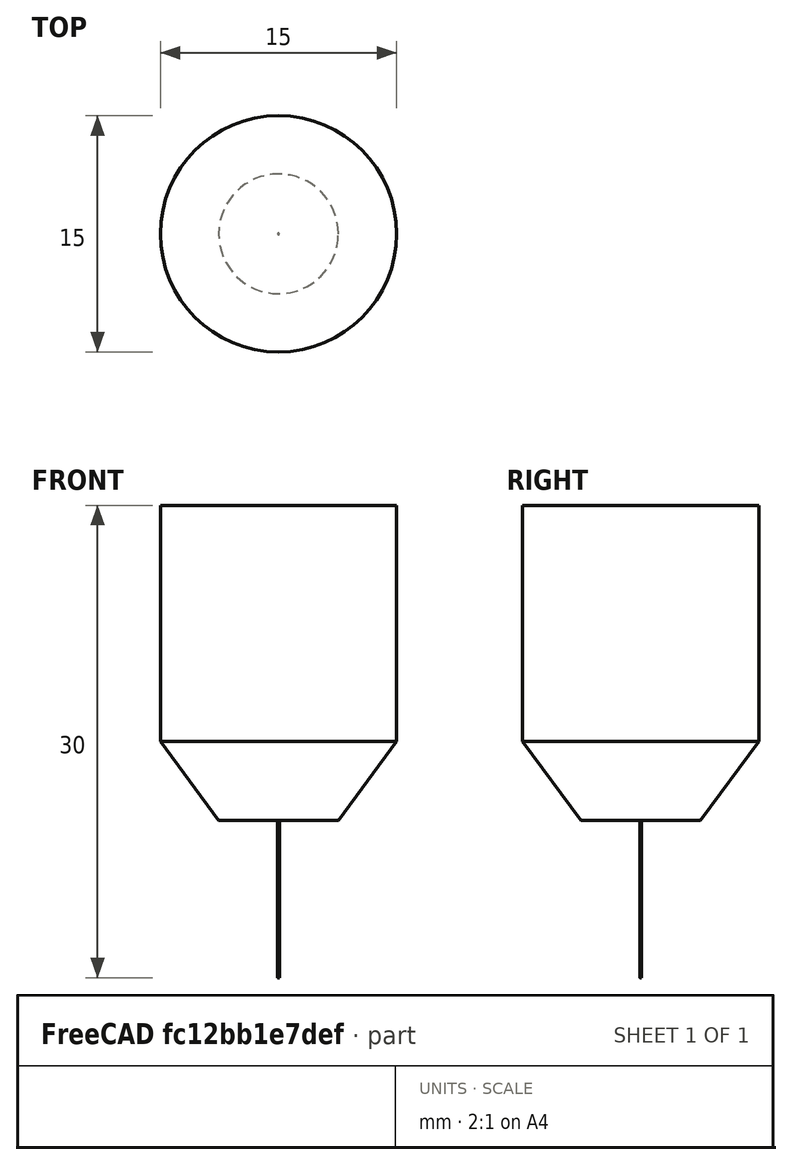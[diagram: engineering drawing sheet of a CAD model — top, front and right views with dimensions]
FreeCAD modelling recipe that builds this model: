
FCSTD DOCUMENT  (FreeCAD 0.20R25177 (Git))
Label: laser
License: All rights reserved
LicenseURL: http://en.wikipedia.org/wiki/All_rights_reserved
objects: Sketcher::SketchObject×1, PartDesign::Revolution×1, App::FeaturePython×1, PartDesign::Body×1
note: 4 computed .brp shape members not serialized (recipe doc carries the construction recipe); baked Part::Feature solids carry a one-line shape summary decoded from their .brp

FEATURE [Sketcher::SketchObject] Sketch
  FullyConstrained = true
  MapMode = 5
  Placement = pos=(0,0,0) rot=(1,0,0;1.5708rad)
  Support = -> [XZ_Plane]
  expr: Constraints[23] = <<Attributes>>.ShankDiameter / 3
  expr: Constraints[15] = <<Attributes>>.CuttingEdgeHeight
  expr: Constraints[22] = <<Attributes>>.ShankDiameter / 4
  expr: Constraints[9] = <<Attributes>>.Diameter
  expr: Constraints[14] = <<Attributes>>.ShankDiameter
  expr: Constraints[10] = <<Attributes>>.Length
  sketch-geometry (9):
    g0: LineSegment StartX=0 StartY=30 StartZ=0 EndX=0 EndY=0 EndZ=0
    g1: LineSegment StartX=0 StartY=0 StartZ=0 EndX=0.05 EndY=0 EndZ=0
    g2: LineSegment StartX=0.05 StartY=0 StartZ=0 EndX=0.05 EndY=10 EndZ=0
    g3: LineSegment StartX=7.5 StartY=30 StartZ=0 EndX=0 EndY=30 EndZ=0
    g4: LineSegment StartX=0.05 StartY=0 StartZ=0 EndX=-0.05 EndY=0 EndZ=0
    g5: LineSegment StartX=3.8 StartY=10 StartZ=0 EndX=0.05 EndY=10 EndZ=0
    g6: LineSegment StartX=-7.5 StartY=30 StartZ=0 EndX=7.5 EndY=30 EndZ=0
    g7: LineSegment StartX=7.5 StartY=30 StartZ=0 EndX=7.5 EndY=15 EndZ=0
    g8: LineSegment StartX=3.8 StartY=10 StartZ=0 EndX=7.5 EndY=15 EndZ=0
  constraints (24):
    c: Vertical(g0)
    c: Coincident(g0,g1)
    c: Horizontal(g1)
    c: Coincident(g1,g2)
    c: Vertical(g2)
    c: Horizontal(g3)
    c: Coincident(g0,g3)
    c: Coincident(g4,g1)
    c: Symmetric(g1,g4,g0)
    c: DistanceX(g4,g4) = 0.1
    c: DistanceY(g2,g3) = 30
    c: Coincident(g2,g5)
    c: Symmetric(g6,g6,g0)
    c: Coincident(g6,g3)
    c: DistanceX(g6,g6) = 15
    c: DistanceY(g2) = 10
    c: Coincident(g0,g-1)
    c: Coincident(g7,g3)
    c: Vertical(g7)
    c: Coincident(g8,g5)
    c: Coincident(g8,g7)
    c: Horizontal(g5)
    c: DistanceX(g5,g5) = 3.75
    c: DistanceY(g5,g7) = 5
FEATURE [PartDesign::Revolution] Revolution
  AllowMultiFace = false
  Angle = 360
  Axis = (0,-2e-16,1)
  Base = (0,0,0)
  Placement = pos=(0,0,0) rot=(1,0,0;1.5708rad)
  Profile = -> Sketch
  ReferenceAxis = -> Sketch [V_Axis]
  Reversed = true
FEATURE [App::FeaturePython] PropertyBag  label="Attributes"  # WARN: FeaturePython — macro-defined, semantics opaque (R4)
  Chipload = 0
  CustomPropertyGroups = Attributes | Shape
  CuttingEdgeHeight = 10
  Diameter = 0.1
  Flutes = 0
  Length = 30
  Material = 0
  ShankDiameter = 15
FEATURE [PartDesign::Body] Body  label="Laser"
  Group = -> [Sketch,Revolution,PropertyBag]
  Origin = -> Origin
  Tip = -> Revolution
